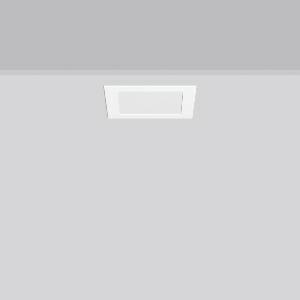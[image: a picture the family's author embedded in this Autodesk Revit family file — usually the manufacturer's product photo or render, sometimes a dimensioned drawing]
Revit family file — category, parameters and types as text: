
# Revit family: toledo_flat_square_e_672242_002_1_dbd0
name_source: partatom
category: Lighting Fixtures
units: mm (PartAtom-declared; Revit-internal decimal feet)

## family parameters
Cut with Voids When Loaded = No
Host = Face
Light Source = No
Part Type = Normal
Room Calculation Point = No
Round Connector Dimension = Use Diameter
Shared = No

## types (1)
- TOLEDO FLAT square E (1 x LED Modul 840, 750 lm, 4000)
    Apparent Load = 8 VA
    CIE Flux Codes = 49 80 96 100 100
    Color Rendering = 80
    Color Temperature = 4000
    Default Elevation = 1800 mm
    Description = Series: TOLEDO FLAT square
Square recessed downlight. For escape route illumination. Housing: die-cast aluminium, powder-coated. Lightguide and diffuser made of non-yellowing plastic (PMMA). Diffuser opal matt plastic. Ceiling installation with spring system. Including separate LED converter with connecting cable 250 mm. Suitable for connection to central battery systems. External driver with simple plug-in locking system. 
Colour: white
Length: 172 mm
Width: 172 mm
Height: 3 mm
Cut-out length: 156 mm
Cut-out width: 156 mm
Recess height: 35 mm
Luminaire: recess height: 31-51 mm
Weight: 423 g
Operating mode: maintained power mode
Lamp: LED
Socket: without socket
Colour temperature: 4000K
Colour rendering index (CRI): 80
System power: 8 W
Rated luminous flux: 750 lm
Luminous flux, emergency: 750 lm
System power, emergency: 8 W
Control gear: Regulated power supply
Protection class: II
Type of protection: IP 54
    Height = 0 mm  [stored 0 ft]
    Lamp = 1 x LED Modul 840
    Lamp Light Flux = 750 lm
    Lamp count = 1
    Length = 172 mm
    Lifetime = 50000 h
    Luminous efficacy = 94 lm/W
    Manufacturer = RZB
    ModVariant = No
    Model = 672242.002.1
    Mounting Place = Ceiling
    Mounting Type = Recessed
    Number of Poles = 1
    OnlyDefault = Yes
    Power Factor = 1
    Product Name = TOLEDO FLAT square E
    Product group = Recessed downlights
    ProductGroupID = 402
    Protection Class = Protection class II
    Protection Degree = IP 40
    RLX_Detail_Level = 1
    RLX_Emergency_Light_Flux = 750 lm
    RLX_Emergency_Type = 3
    RLX_Emergency_Type_DB = Yes
    RlxData = <blob elided: 9993 chars, md5=72c1adeb>
    Socket = socket
    Standby Power = 0 W
    System Light Flux = 750 lm
    System Power = 8 W
    Type Comments = Product without accessories
    Type Image = 901486.002.jpg
    URL = http://relux.com
    VarID = ---
    Voltage = 230 V
    Voltage Range = 220-240 V
    Weight = 0.00 kg
    Width = 172 mm

note: [stored X ft] marks values corroborated as IEEE doubles in the binary element streams (Revit-internal decimal feet)

## geometry (parser evidence)
native form markers: Sweep x10
no freeform markers — native parametric forms only
